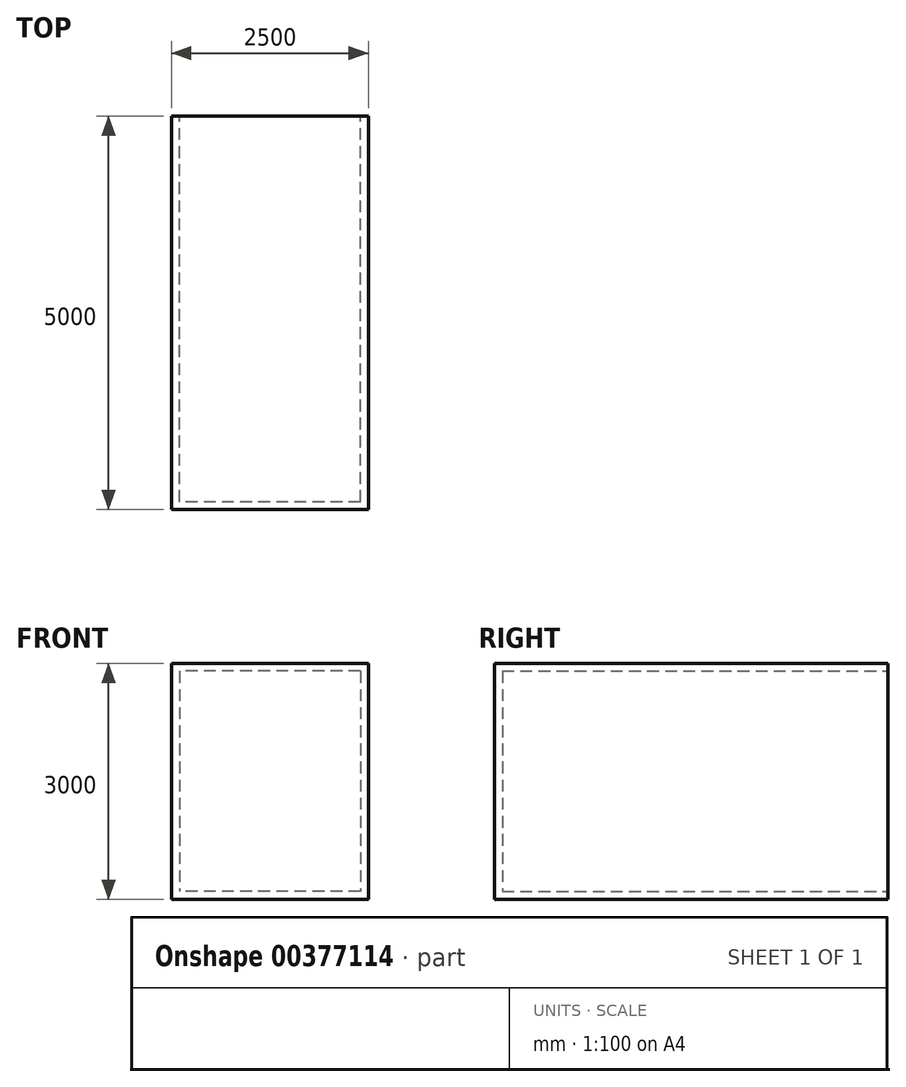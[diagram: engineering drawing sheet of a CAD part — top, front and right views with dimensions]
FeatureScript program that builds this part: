
annotation { "Feature Type Name" : "Feature", "Feature Type Description" : "" }
export const myFeature = defineFeature(function(context is Context, id is Id, definition is map)
    precondition{}
    {
        {
            assignVariable(context, id + "F0", {"name" : "thick", "anyValue" : 100 * mm});
        }
        {
            assignVariable(context, id + "F1", {"name" : "deep", "anyValue" : 5000 * mm});
        }
        {
            var Q0;
            Q0=qCreatedBy(makeId("Front.planeOp"),FACE);
            var sketch = newSketch(context, id + "F2", { "sketchPlane" : qUnion([Q0])});
            skLineSegment(sketch, "E0.bottom", {"start": v(-1250, 1500) * mm, "end": v(1250, 1500) * mm});
            skLineSegment(sketch, "E0.top", {"start": v(-1250, -1500) * mm, "end": v(1250, -1500) * mm});
            skLineSegment(sketch, "E0.left", {"start": v(-1250, 1500) * mm, "end": v(-1250, -1500) * mm});
            skLineSegment(sketch, "E0.right", {"start": v(1250, 1500) * mm, "end": v(1250, -1500) * mm});
            skPoint(sketch, "E0.middle", {"position": v(0, 0) * mm});
            skSolve(sketch);
        }
        {
            var Q0;
            Q0 = qSketchRegion(id + "F2", true);
            extrude(context, id + "F3", {"entities" : qUnion([Q0]), "oppositeDirection" : true, "depth" : getVariable(context, 'deep')});
        }
        {
            var Q0;
            Q0=makeQuery(id+"F3.opExtrude","CAP_FACE",FACE,{"disambiguationData":[OSD([sQuery(id+"F2.wireOp",EDGE,"E0.bottom"),sQuery(id+"F2.wireOp",EDGE,"E0.top"),sQuery(id+"F2.wireOp",EDGE,"E0.left"),sQuery(id+"F2.wireOp",EDGE,"E0.right")])],"isStart":false});
            var sketch = newSketch(context, id + "F4", { "sketchPlane" : qUnion([Q0])});
            skLineSegment(sketch, "E1.bottom", {"start": v(-1150, 1400) * mm, "end": v(1150, 1400) * mm});
            skLineSegment(sketch, "E1.top", {"start": v(-1150, -1400) * mm, "end": v(1150, -1400) * mm});
            skLineSegment(sketch, "E1.left", {"start": v(-1150, 1400) * mm, "end": v(-1150, -1400) * mm});
            skLineSegment(sketch, "E1.right", {"start": v(1150, 1400) * mm, "end": v(1150, -1400) * mm});
            skPoint(sketch, "E1.middle", {"position": v(0, 0) * mm});
            skSolve(sketch);
        }
        {
            var Q0;
            Q0 = qSketchRegion(id + "F4", true);
            extrude(context, id + "F5", {"entities" : qUnion([Q0]), "operationType" : NewBodyOperationType.REMOVE, "oppositeDirection" : true, "depth" : getVariable(context, 'deep') - getVariable(context, 'thick')});
        }
    });
